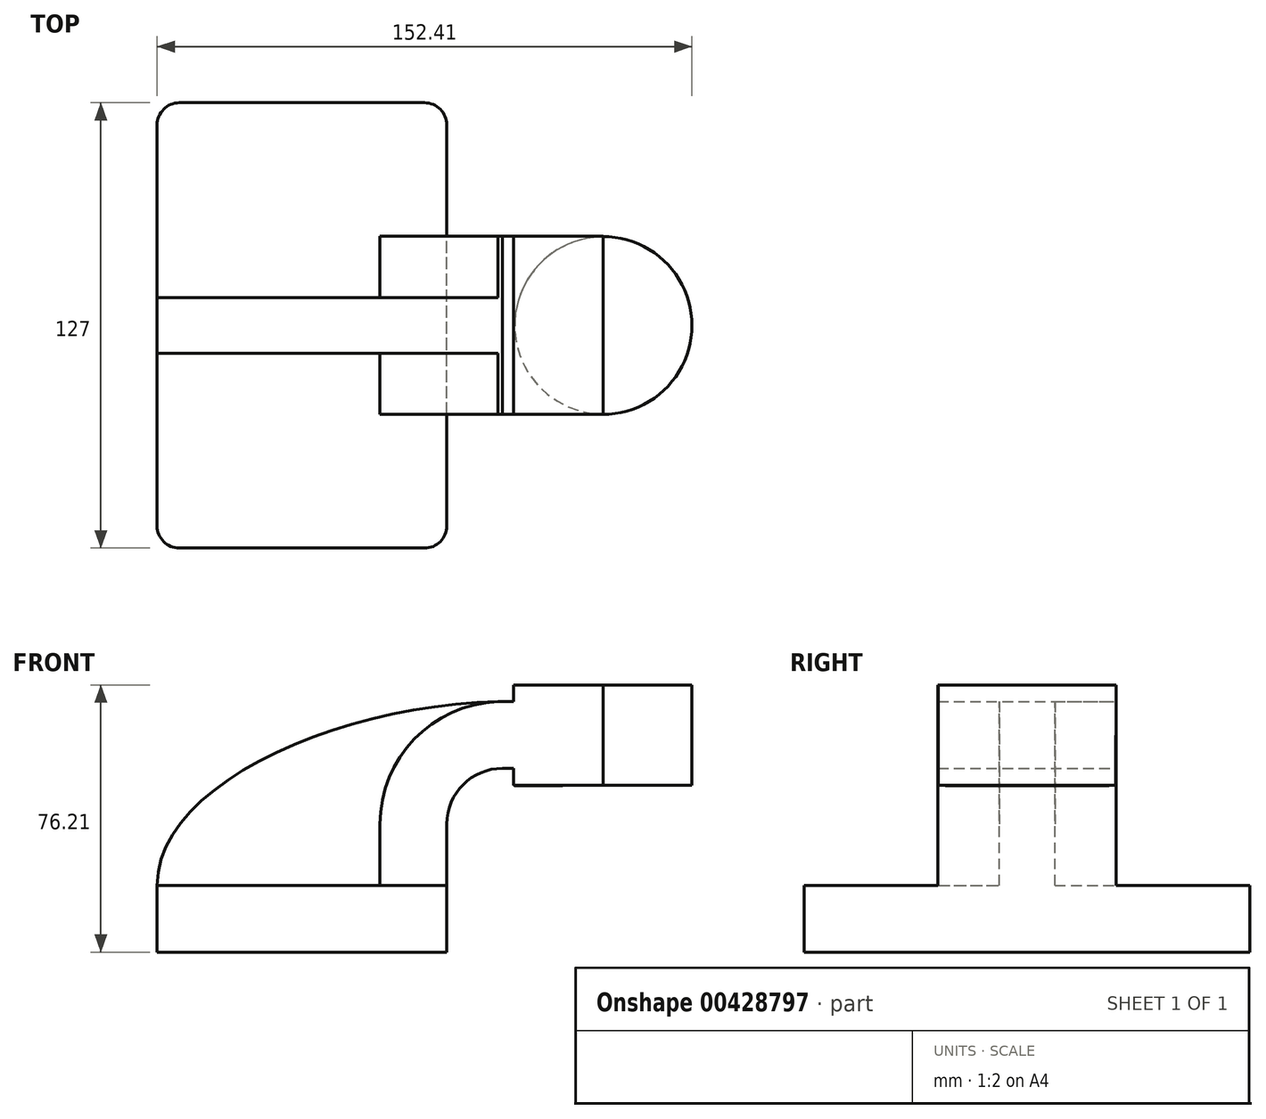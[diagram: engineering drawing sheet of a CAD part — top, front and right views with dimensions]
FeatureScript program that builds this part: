
annotation { "Feature Type Name" : "Feature", "Feature Type Description" : "" }
export const myFeature = defineFeature(function(context is Context, id is Id, definition is map)
    precondition{}
    {
        {
            var Q0;
            Q0=qCreatedBy(makeId("Front.planeOp"),FACE);
            var sketch = newSketch(context, id + "F0", { "sketchPlane" : qUnion([Q0])});
            skLineSegment(sketch, "E0.bottom", {"start": v(-41.27, -9.53) * mm, "end": v(41.28, -9.53) * mm});
            skLineSegment(sketch, "E0.top", {"start": v(-41.28, 9.53) * mm, "end": v(41.28, 9.53) * mm});
            skLineSegment(sketch, "E0.left", {"start": v(-41.28, -9.53) * mm, "end": v(-41.28, 9.53) * mm});
            skLineSegment(sketch, "E0.right", {"start": v(41.28, -9.53) * mm, "end": v(41.28, 9.53) * mm});
            skPoint(sketch, "E0.middle", {"position": v(0, 0) * mm});
            skLineSegment(sketch, "E1.bottom", {"start": v(60.32, 66.67) * mm, "end": v(111.12, 66.67) * mm});
            skLineSegment(sketch, "E1.top", {"start": v(60.33, 38.1) * mm, "end": v(111.12, 38.1) * mm});
            skLineSegment(sketch, "E1.left", {"start": v(60.32, 66.67) * mm, "end": v(60.33, 38.1) * mm});
            skLineSegment(sketch, "E1.right", {"start": v(111.12, 66.67) * mm, "end": v(111.12, 38.1) * mm});
            skPoint(sketch, "E1.middle", {"position": v(85.72, 52.39) * mm});
            skLineSegment(sketch, "E2", {"start": v(41.28, 9.53) * mm, "end": v(41.28, 27) * mm});
            skArc(sketch, "E3", {"start": v(41.27, 27) * mm, "mid": v(45.92, 38.23) * mm, "end": v(57.15, 42.88) * mm});
            skLineSegment(sketch, "E4", {"start": v(85.86, 42.88) * mm, "end": v(57.15, 42.88) * mm});
            skLineSegment(sketch, "E5.0", {"start": v(85.76, 61.93) * mm, "end": v(57.15, 61.93) * mm});
            skArc(sketch, "E5.1", {"start": v(22.22, 27) * mm, "mid": v(32.45, 51.7) * mm, "end": v(57.15, 61.93) * mm});
            skLineSegment(sketch, "E5.2", {"start": v(22.22, 9.53) * mm, "end": v(22.22, 27) * mm});
            skFitSpline(sketch, "E6", {"points": [v(-41.27, 9.53) * mm, v(57.15, 61.93) * mm], "startDerivative": vector(0.32, 87.57) * mm, "endDerivative": vector(138.05, 2.03) * mm});
            skLineSegment(sketch, "E7", {"start": v(85.76, 66.67) * mm, "end": v(85.86, 38.1) * mm});
            skSolve(sketch);
        }
        {
            var Q0;
            Q0=makeQuery(id+"F0.imprint","IMPRINT",FACE,{"disambiguationData":[TD([[makeQuery(id+"F0.imprint","IMPRINT",EDGE,{"derivedFrom":sQuery(id+"F0.wireOp",EDGE,"E0.bottom")}),1.0]])]});
            extrude(context, id + "F1", {"entities" : qUnion([Q0]), "endBound" : BoundingType.SYMMETRIC, "depth" : 127 * mm});
        }
        {
            var Q0;
            {var subQ1=sQuery(id+"F0.wireOp",EDGE,"E2");Q0=makeQuery(id+"F0.imprint","IMPRINT",FACE,{"disambiguationData":[TD([[makeQuery(id+"F0.imprint","IMPRINT",EDGE,{"derivedFrom":subQ1}),1.0]])]});}
            var Q1;
            {var subQ0=sQuery(id+"F0.wireOp",EDGE,"E1.left");var subQ1=sQuery(id+"F0.wireOp",EDGE,"E1.bottom");var subQ2=makeQuery(id+"F0.imprint","INTERSECT",VERTEX,{"derivedFrom":[subQ1,subQ0]});Q1=makeQuery(id+"F0.imprint","IMPRINT",FACE,{"disambiguationData":[TD([[makeQuery(id+"F0.imprint","IMPRINT",EDGE,{"disambiguationData":[TD([[subQ2,-1.0]])],"derivedFrom":subQ1}),-1.0]])]});}
            var Q2;
            {var subQ0=sQuery(id+"F0.wireOp",EDGE,"E1.left");var subQ1=sQuery(id+"F0.wireOp",EDGE,"E1.top");var subQ2=makeQuery(id+"F0.imprint","INTERSECT",VERTEX,{"derivedFrom":[subQ1,subQ0]});Q2=makeQuery(id+"F0.imprint","IMPRINT",FACE,{"disambiguationData":[TD([[makeQuery(id+"F0.imprint","IMPRINT",EDGE,{"disambiguationData":[TD([[subQ2,-1.0]])],"derivedFrom":subQ1}),1.0]])]});}
            extrude(context, id + "F2", {"entities" : qUnion([Q0, Q1, Q2]), "operationType" : NewBodyOperationType.ADD, "endBound" : BoundingType.SYMMETRIC, "depth" : 50.8 * mm});
        }
        {
            var Q0;
            {var subQ3=sQuery(id+"F0.wireOp",EDGE,"E5.2");Q0=makeQuery(id+"F0.imprint","IMPRINT",FACE,{"disambiguationData":[TD([[makeQuery(id+"F0.imprint","IMPRINT",EDGE,{"derivedFrom":subQ3}),1.0]])]});}
            extrude(context, id + "F3", {"entities" : qUnion([Q0]), "operationType" : NewBodyOperationType.ADD, "endBound" : BoundingType.SYMMETRIC, "depth" : 15.88 * mm});
        }
        {
            var Q0;
            {var subQ0=sQuery(id+"F0.wireOp",EDGE,"E1.right");Q0=makeQuery(id+"F0.imprint","IMPRINT",FACE,{"disambiguationData":[TD([[makeQuery(id+"F0.imprint","IMPRINT",EDGE,{"derivedFrom":subQ0}),-1.0]])]});}
            var Q1;
            Q1=sQuery(id+"F0.wireOp",EDGE,"E7");
            revolve(context, id + "F4", {"operationType" : NewBodyOperationType.ADD, "entities" : qUnion([Q0]), "axis" : qUnion([Q1]), "revolveType" : RevolveType.FULL});
        }
        {
            var Q0;
            Q0=makeQuery(id+"F1.opExtrude","CAP_EDGE",EDGE,{"disambiguationData":[OSD([sQuery(id+"F0.wireOp",EDGE,"E0.right")])],"isStart":false});
            var Q1;
            Q1=makeQuery(id+"F1.opExtrude","CAP_EDGE",EDGE,{"disambiguationData":[OSD([sQuery(id+"F0.wireOp",EDGE,"E0.right")])],"isStart":true});
            var Q2;
            Q2=makeQuery(id+"F1.opExtrude","CAP_EDGE",EDGE,{"disambiguationData":[OSD([sQuery(id+"F0.wireOp",EDGE,"E0.left")])],"isStart":true});
            var Q3;
            Q3=makeQuery(id+"F1.opExtrude","CAP_EDGE",EDGE,{"disambiguationData":[OSD([sQuery(id+"F0.wireOp",EDGE,"E0.left")])],"isStart":false});
            fillet(context, id + "F5", {"entities" : qUnion([Q0, Q1, Q2, Q3]), "radius" : 6.35 * mm, "tangentPropagation" : true, "allowEdgeOverflow" : false});
        }
    });
